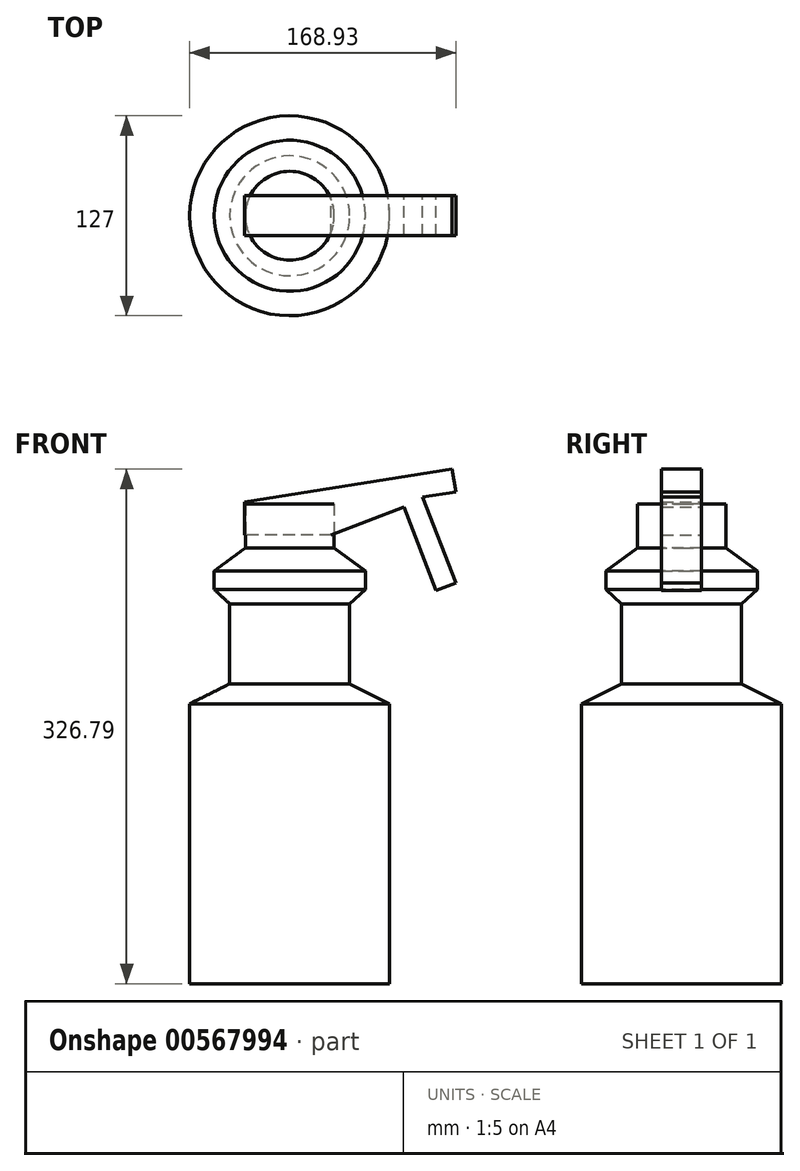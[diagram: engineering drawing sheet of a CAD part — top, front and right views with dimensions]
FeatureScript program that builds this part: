
annotation { "Feature Type Name" : "Feature", "Feature Type Description" : "" }
export const myFeature = defineFeature(function(context is Context, id is Id, definition is map)
    precondition{}
    {
        {
            var Q0;
            Q0=qCreatedBy(makeId("Front.planeOp"),FACE);
            var sketch = newSketch(context, id + "F0", { "sketchPlane" : qUnion([Q0])});
            skLineSegment(sketch, "E0", {"start": v(0, 0) * mm, "end": v(0, 304.8) * mm});
            skLineSegment(sketch, "E1", {"start": v(0, 0) * mm, "end": v(63.5, 0) * mm});
            skLineSegment(sketch, "E2", {"start": v(63.5, 0) * mm, "end": v(63.5, 177.8) * mm});
            skLineSegment(sketch, "E3", {"start": v(63.5, 177.8) * mm, "end": v(38.1, 190.5) * mm});
            skLineSegment(sketch, "E4", {"start": v(38.1, 190.5) * mm, "end": v(38.1, 241.3) * mm});
            skLineSegment(sketch, "E5", {"start": v(38.1, 241.3) * mm, "end": v(48, 250.42) * mm});
            skLineSegment(sketch, "E6", {"start": v(48, 250.42) * mm, "end": v(48, 262.25) * mm});
            skLineSegment(sketch, "E7", {"start": v(48, 262.25) * mm, "end": v(28.24, 276.7) * mm});
            skLineSegment(sketch, "E8", {"start": v(28.24, 276.7) * mm, "end": v(28.24, 304.8) * mm});
            skLineSegment(sketch, "E9", {"start": v(28.24, 304.8) * mm, "end": v(0, 304.8) * mm});
            skSolve(sketch);
        }
        {
            var Q0;
            Q0 = qSketchRegion(id + "F0", true);
            var Q1;
            Q1=sQuery(id+"F0.wireOp",EDGE,"E0");
            revolve(context, id + "F1", {"entities" : qUnion([Q0]), "axis" : qUnion([Q1]), "revolveType" : RevolveType.FULL});
        }
        {
            var Q0;
            Q0=qCreatedBy(makeId("Front.planeOp"),FACE);
            var sketch = newSketch(context, id + "F2", { "sketchPlane" : qUnion([Q0])});
            skLineSegment(sketch, "E10", {"start": v(-28.83, 306.03) * mm, "end": v(103.16, 326.79) * mm});
            skLineSegment(sketch, "E11", {"start": v(103.16, 326.79) * mm, "end": v(105.43, 312.38) * mm});
            skLineSegment(sketch, "E12", {"start": v(105.43, 312.38) * mm, "end": v(84.42, 309.08) * mm});
            skLineSegment(sketch, "E13", {"start": v(84.42, 309.08) * mm, "end": v(105.43, 254.57) * mm});
            skLineSegment(sketch, "E14", {"start": v(105.43, 254.57) * mm, "end": v(93, 249.78) * mm});
            skLineSegment(sketch, "E15", {"start": v(93, 249.78) * mm, "end": v(72.53, 302.88) * mm});
            skLineSegment(sketch, "E16", {"start": v(72.53, 302.88) * mm, "end": v(26.3, 285.06) * mm});
            skLineSegment(sketch, "E17", {"start": v(26.3, 285.06) * mm, "end": v(-28.83, 285.06) * mm});
            skLineSegment(sketch, "E18", {"start": v(-28.83, 285.06) * mm, "end": v(-28.83, 306.03) * mm});
            skSolve(sketch);
        }
        {
            var Q0;
            Q0 = qSketchRegion(id + "F2", true);
            var Q1;
            Q1=sQuery(id+"F2.wireOp",EDGE,"E10");
            var Q2;
            Q2=sQuery(id+"F2.wireOp",EDGE,"E11");
            var Q3;
            Q3=sQuery(id+"F2.wireOp",EDGE,"E13");
            var Q4;
            Q4=sQuery(id+"F2.wireOp",EDGE,"E15");
            var Q5;
            Q5=sQuery(id+"F2.wireOp",EDGE,"E16");
            var Q6;
            Q6=sQuery(id+"F2.wireOp",EDGE,"E12");
            var Q7;
            Q7=sQuery(id+"F2.wireOp",EDGE,"E14");
            extrude(context, id + "F3", {"entities" : qUnion([Q0]), "surfaceEntities" : qUnion([Q1, Q2, Q3, Q4, Q5, Q6, Q7]), "depth" : 12.7 * mm, "offsetDistance" : 25.4 * mm, "hasSecondDirection" : true, "secondDirectionOppositeDirection" : true, "secondDirectionDepth" : 12.7 * mm});
        }
    });
